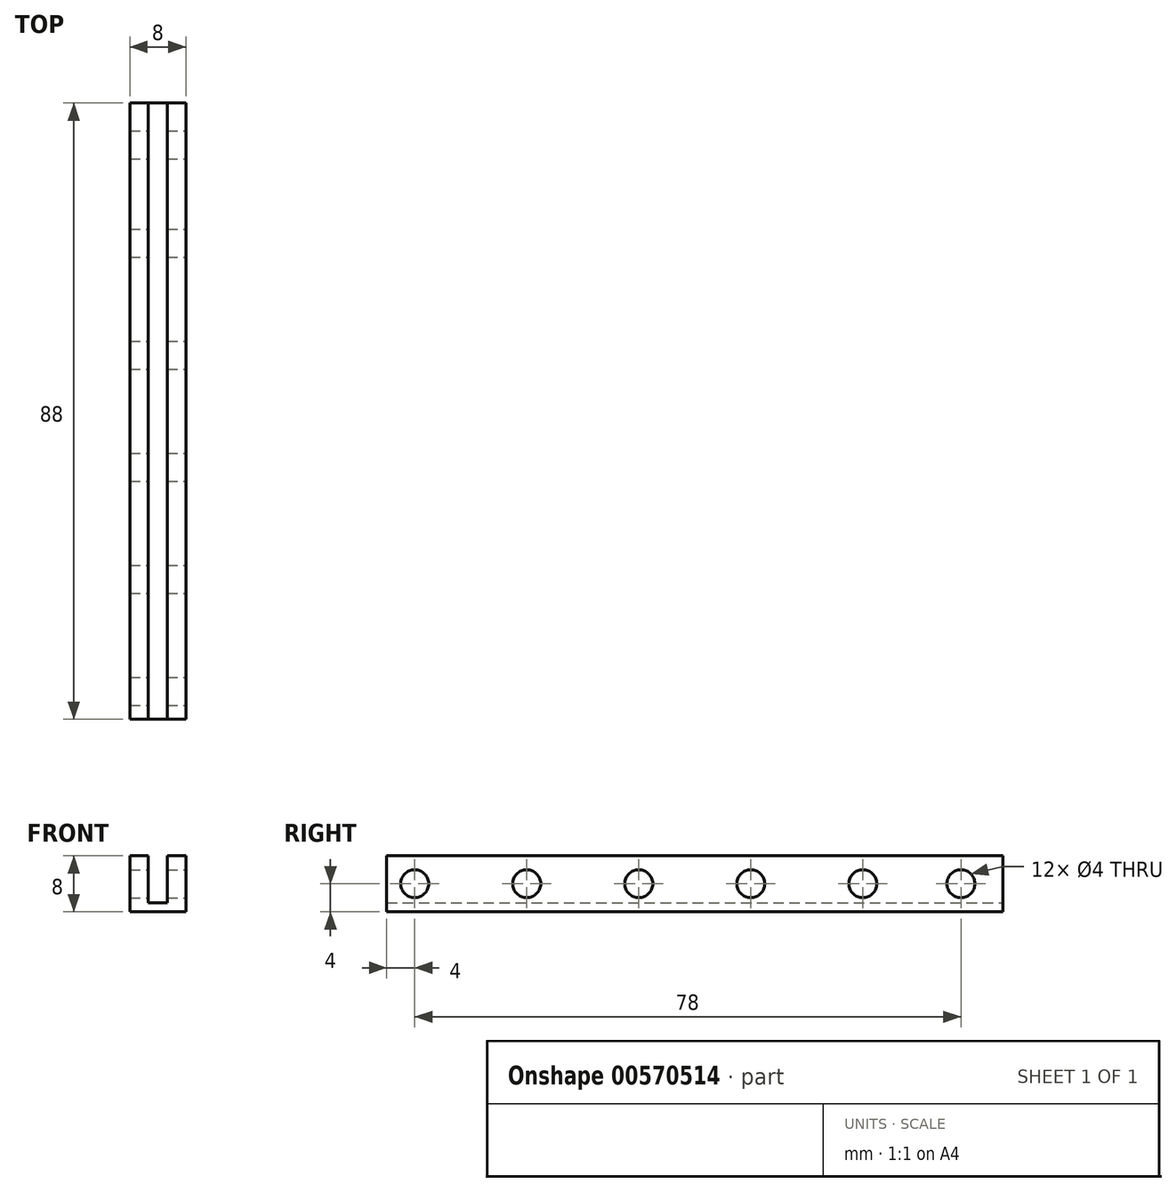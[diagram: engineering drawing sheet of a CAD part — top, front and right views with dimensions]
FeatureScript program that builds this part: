
annotation { "Feature Type Name" : "Feature", "Feature Type Description" : "" }
export const myFeature = defineFeature(function(context is Context, id is Id, definition is map)
    precondition{}
    {
        {
            var Q0;
            Q0=qCreatedBy(makeId("Front.planeOp"),FACE);
            var sketch = newSketch(context, id + "F0", { "sketchPlane" : qUnion([Q0])});
            skLineSegment(sketch, "E0.bottom", {"start": v(-4, 4) * mm, "end": v(4, 4) * mm});
            skLineSegment(sketch, "E0.top", {"start": v(-4, -4) * mm, "end": v(4, -4) * mm});
            skLineSegment(sketch, "E0.left", {"start": v(-4, 4) * mm, "end": v(-4, -4) * mm});
            skLineSegment(sketch, "E0.right", {"start": v(4, 4) * mm, "end": v(4, -4) * mm});
            skPoint(sketch, "E0.middle", {"position": v(0, 0) * mm});
            skLineSegment(sketch, "E1.bottom", {"start": v(-1.34, 10.75) * mm, "end": v(1.34, 10.75) * mm});
            skLineSegment(sketch, "E1.top", {"start": v(-1.34, -2.75) * mm, "end": v(1.34, -2.75) * mm});
            skLineSegment(sketch, "E1.left", {"start": v(-1.34, 10.75) * mm, "end": v(-1.34, -2.75) * mm});
            skLineSegment(sketch, "E1.right", {"start": v(1.34, 10.75) * mm, "end": v(1.34, -2.75) * mm});
            skPoint(sketch, "E1.middle", {"position": v(0, 4) * mm});
            skSolve(sketch);
        }
        {
            var Q0;
            Q0=makeQuery(id+"F0.imprint","IMPRINT",FACE,{"disambiguationData":[TD([[makeQuery(id+"F0.imprint","IMPRINT",EDGE,{"derivedFrom":sQuery(id+"F0.wireOp",EDGE,"E0.top")}),1.0]])]});
            extrude(context, id + "F1", {"entities" : qUnion([Q0]), "depth" : 88 * mm, "offsetDistance" : 25 * mm});
        }
        {
            var Q0;
            Q0=makeQuery(id+"F1.opExtrude","SWEPT_FACE",FACE,{"disambiguationData":[OSD([sQuery(id+"F0.wireOp",EDGE,"E0.right")])]});
            var sketch = newSketch(context, id + "F2", { "sketchPlane" : qUnion([Q0])});
            skCircle(sketch, "E2", {"center": v(-84, 0) * mm, "radius": 2 * mm});
            skCircle(sketch, "E3", {"center": v(-68, 0) * mm, "radius": 2 * mm});
            skCircle(sketch, "E4", {"center": v(-52, 0) * mm, "radius": 2 * mm});
            skCircle(sketch, "E5", {"center": v(-36, 0) * mm, "radius": 2 * mm});
            skCircle(sketch, "E6", {"center": v(-20, 0) * mm, "radius": 2 * mm});
            skCircle(sketch, "E7", {"center": v(-6, 0) * mm, "radius": 2 * mm});
            skSolve(sketch);
        }
        {
            var Q0;
            Q0=makeQuery(id+"F2.imprint","IMPRINT",FACE,{"disambiguationData":[TD([[makeQuery(id+"F2.imprint","IMPRINT",EDGE,{"derivedFrom":sQuery(id+"F2.wireOp",EDGE,"E2")}),1.0]])]});
            var Q1;
            Q1=makeQuery(id+"F2.imprint","IMPRINT",FACE,{"disambiguationData":[TD([[makeQuery(id+"F2.imprint","IMPRINT",EDGE,{"derivedFrom":sQuery(id+"F2.wireOp",EDGE,"E3")}),1.0]])]});
            var Q2;
            Q2=makeQuery(id+"F2.imprint","IMPRINT",FACE,{"disambiguationData":[TD([[makeQuery(id+"F2.imprint","IMPRINT",EDGE,{"derivedFrom":sQuery(id+"F2.wireOp",EDGE,"E4")}),1.0]])]});
            var Q3;
            Q3=makeQuery(id+"F2.imprint","IMPRINT",FACE,{"disambiguationData":[TD([[makeQuery(id+"F2.imprint","IMPRINT",EDGE,{"derivedFrom":sQuery(id+"F2.wireOp",EDGE,"E5")}),1.0]])]});
            var Q4;
            Q4=makeQuery(id+"F2.imprint","IMPRINT",FACE,{"disambiguationData":[TD([[makeQuery(id+"F2.imprint","IMPRINT",EDGE,{"derivedFrom":sQuery(id+"F2.wireOp",EDGE,"E6")}),1.0]])]});
            var Q5;
            Q5=makeQuery(id+"F2.imprint","IMPRINT",FACE,{"disambiguationData":[TD([[makeQuery(id+"F2.imprint","IMPRINT",EDGE,{"derivedFrom":sQuery(id+"F2.wireOp",EDGE,"E7")}),1.0]])]});
            extrude(context, id + "F3", {"entities" : qUnion([Q0, Q1, Q2, Q3, Q4, Q5]), "operationType" : NewBodyOperationType.REMOVE, "oppositeDirection" : true, "depth" : 8.1 * mm, "offsetDistance" : 25 * mm});
        }
    });
